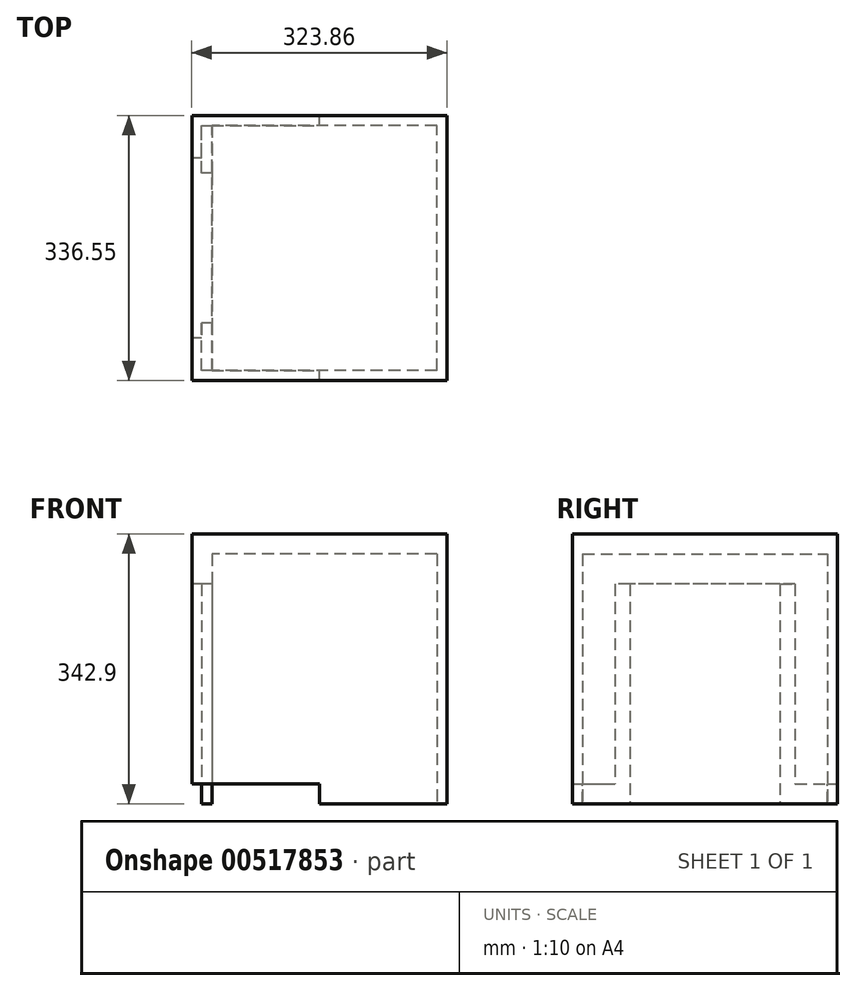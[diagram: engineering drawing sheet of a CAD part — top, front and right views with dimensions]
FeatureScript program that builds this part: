
annotation { "Feature Type Name" : "Feature", "Feature Type Description" : "" }
export const myFeature = defineFeature(function(context is Context, id is Id, definition is map)
    precondition{}
    {
        {
            var Q0;
            Q0=qCreatedBy(makeId("Top.planeOp"),FACE);
            var sketch = newSketch(context, id + "F0", { "sketchPlane" : qUnion([Q0])});
            skLineSegment(sketch, "E0.bottom", {"start": v(-161.92, 172.99) * mm, "end": v(161.92, 172.99) * mm});
            skLineSegment(sketch, "E0.top", {"start": v(-161.92, -163.56) * mm, "end": v(161.92, -163.56) * mm});
            skLineSegment(sketch, "E0.left", {"start": v(-161.92, 172.99) * mm, "end": v(-161.92, -163.56) * mm});
            skLineSegment(sketch, "E0.right", {"start": v(161.92, 172.99) * mm, "end": v(161.92, -163.56) * mm});
            skLineSegment(sketch, "E1", {"start": v(0, -163.56) * mm, "end": v(0, 172.99) * mm});
            skSolve(sketch);
        }
        {
            var Q0;
            Q0 = qSketchRegion(id + "F0", true);
            extrude(context, id + "F1", {"entities" : qUnion([Q0]), "depth" : 342.9 * mm, "offsetDistance" : 25.4 * mm});
        }
        {
            var Q0;
            Q0=makeQuery(id+"F1.opExtrude","CAP_FACE",FACE,{"disambiguationData":[OSD([sQuery(id+"F0.wireOp",EDGE,"E0.bottom"),sQuery(id+"F0.wireOp",EDGE,"E0.top"),sQuery(id+"F0.wireOp",EDGE,"E0.left"),sQuery(id+"F0.wireOp",EDGE,"E0.right")])],"isStart":true});
            var sketch = newSketch(context, id + "F2", { "sketchPlane" : qUnion([Q0])});
            skPoint(sketch, "E2.middle", {"position": v(0, 0) * mm});
            skLineSegment(sketch, "E3.bottom", {"start": v(149.22, 150.86) * mm, "end": v(-136.53, 150.86) * mm});
            skLineSegment(sketch, "E3.top", {"start": v(149.23, -160.29) * mm, "end": v(-136.52, -160.29) * mm});
            skLineSegment(sketch, "E3.left", {"start": v(149.22, 150.86) * mm, "end": v(149.23, -160.29) * mm});
            skLineSegment(sketch, "E3.right", {"start": v(-136.53, 150.86) * mm, "end": v(-136.52, -160.29) * mm});
            skSolve(sketch);
        }
        {
            var Q0;
            Q0 = qSketchRegion(id + "F2", true);
            extrude(context, id + "F3", {"entities" : qUnion([Q0]), "operationType" : NewBodyOperationType.REMOVE, "oppositeDirection" : true, "depth" : 317.5 * mm, "offsetDistance" : 25.4 * mm});
        }
        {
            var Q0;
            Q0=makeQuery(id+"F1.opExtrude","SWEPT_FACE",FACE,{"disambiguationData":[OSD([sQuery(id+"F0.wireOp",EDGE,"E0.left")])]});
            var sketch = newSketch(context, id + "F4", { "sketchPlane" : qUnion([Q0])});
            skLineSegment(sketch, "E4.bottom", {"start": v(-87.26, 222.25) * mm, "end": v(77.84, 222.25) * mm});
            skLineSegment(sketch, "E4.top", {"start": v(-87.26, 0) * mm, "end": v(77.84, 0) * mm});
            skLineSegment(sketch, "E4.left", {"start": v(-87.26, 222.25) * mm, "end": v(-87.26, 0) * mm});
            skLineSegment(sketch, "E4.right", {"start": v(77.84, 222.25) * mm, "end": v(77.84, 0) * mm});
            skSolve(sketch);
        }
        {
            var Q0;
            Q0 = qSketchRegion(id + "F4", true);
            extrude(context, id + "F5", {"entities" : qUnion([Q0]), "operationType" : NewBodyOperationType.REMOVE, "oppositeDirection" : true, "depth" : 50.8 * mm, "offsetDistance" : 25.4 * mm});
        }
        {
            var Q0;
            Q0=makeQuery(id+"F1.opExtrude","SWEPT_FACE",FACE,{"disambiguationData":[OSD([sQuery(id+"F0.wireOp",EDGE,"E0.left")])]});
            var sketch = newSketch(context, id + "F6", { "sketchPlane" : qUnion([Q0])});
            skLineSegment(sketch, "E5.bottom", {"start": v(-119.01, 279.4) * mm, "end": v(109.59, 279.4) * mm});
            skLineSegment(sketch, "E5.top", {"start": v(-119.01, 0) * mm, "end": v(109.59, 0) * mm});
            skLineSegment(sketch, "E5.left", {"start": v(-119.01, 279.4) * mm, "end": v(-119.01, 0) * mm});
            skLineSegment(sketch, "E5.right", {"start": v(109.59, 279.4) * mm, "end": v(109.59, 0) * mm});
            skSolve(sketch);
        }
        {
            var Q0;
            Q0 = qSketchRegion(id + "F6", true);
            extrude(context, id + "F7", {"entities" : qUnion([Q0]), "operationType" : NewBodyOperationType.REMOVE, "oppositeDirection" : true, "depth" : 76.2 * mm, "offsetDistance" : 25.4 * mm});
        }
        {
            var Q0;
            Q0=qCreatedBy(makeId("Right.planeOp"),FACE);
            var sketch = newSketch(context, id + "F8", { "sketchPlane" : qUnion([Q0])});
            skLineSegment(sketch, "E6.bottom", {"start": v(-172.3, 0) * mm, "end": v(183.3, 0) * mm});
            skLineSegment(sketch, "E6.top", {"start": v(-172.3, 25.4) * mm, "end": v(183.3, 25.4) * mm});
            skLineSegment(sketch, "E6.left", {"start": v(-172.3, 0) * mm, "end": v(-172.3, 25.4) * mm});
            skLineSegment(sketch, "E6.right", {"start": v(183.3, 0) * mm, "end": v(183.3, 25.4) * mm});
            skSolve(sketch);
        }
        {
            var Q0;
            Q0 = qSketchRegion(id + "F8", true);
            extrude(context, id + "F9", {"entities" : qUnion([Q0]), "operationType" : NewBodyOperationType.REMOVE, "oppositeDirection" : true, "depth" : 203.2 * mm, "offsetDistance" : 25.4 * mm});
        }
        {
            var Q0;
            Q0=makeQuery(id+"F7.boolean.opBoolean","COPY",FACE,{"derivedFrom":makeQuery(id+"F7.opExtrude","SWEPT_FACE",FACE,{"disambiguationData":[OSD([sQuery(id+"F6.wireOp",EDGE,"E5.left")])]})});
            var sketch = newSketch(context, id + "F10", { "sketchPlane" : qUnion([Q0])});
            skLineSegment(sketch, "E7.bottom", {"start": v(-136.52, 279.4) * mm, "end": v(-149.23, 279.4) * mm});
            skLineSegment(sketch, "E7.top", {"start": v(-136.52, 25.4) * mm, "end": v(-149.22, 25.4) * mm});
            skLineSegment(sketch, "E7.left", {"start": v(-136.52, 279.4) * mm, "end": v(-136.52, 25.4) * mm});
            skLineSegment(sketch, "E7.right", {"start": v(-149.23, 279.4) * mm, "end": v(-149.22, 25.4) * mm});
            skSolve(sketch);
        }
        {
            var Q0;
            Q0=makeQuery(id+"F7.boolean.opBoolean","COPY",FACE,{"derivedFrom":makeQuery(id+"F7.opExtrude","SWEPT_FACE",FACE,{"disambiguationData":[OSD([sQuery(id+"F6.wireOp",EDGE,"E5.right")])]})});
            var sketch = newSketch(context, id + "F11", { "sketchPlane" : qUnion([Q0])});
            skLineSegment(sketch, "E8.bottom", {"start": v(136.52, 279.4) * mm, "end": v(149.22, 279.4) * mm});
            skLineSegment(sketch, "E8.top", {"start": v(136.52, 25.4) * mm, "end": v(149.22, 25.4) * mm});
            skLineSegment(sketch, "E8.left", {"start": v(136.52, 279.4) * mm, "end": v(136.52, 25.4) * mm});
            skLineSegment(sketch, "E8.right", {"start": v(149.22, 279.4) * mm, "end": v(149.22, 25.4) * mm});
            skSolve(sketch);
        }
        {
            var Q0;
            Q0=makeQuery(id+"F10.imprint","IMPRINT",FACE,{"disambiguationData":[TD([[makeQuery(id+"F10.imprint","IMPRINT",EDGE,{"derivedFrom":sQuery(id+"F10.wireOp",EDGE,"E7.bottom")}),1.0]])]});
            extrude(context, id + "F12", {"entities" : qUnion([Q0]), "operationType" : NewBodyOperationType.ADD, "depth" : 19.05 * mm, "offsetDistance" : 25.4 * mm});
        }
        {
            var Q0;
            Q0=makeQuery(id+"F11.imprint","IMPRINT",FACE,{"disambiguationData":[TD([[makeQuery(id+"F11.imprint","IMPRINT",EDGE,{"derivedFrom":sQuery(id+"F11.wireOp",EDGE,"E8.bottom")}),-1.0]])]});
            var sketch = newSketch(context, id + "F13", { "sketchPlane" : qUnion([Q0])});
            skSolve(sketch);
        }
        {
            var Q0;
            Q0=makeQuery(id+"F13.imprint","IMPRINT",FACE,{"disambiguationData":[TD([[makeQuery(id+"F13.imprint","IMPRINT",EDGE,{"derivedFrom":makeQuery(id+"F11.imprint","IMPRINT",EDGE,{"derivedFrom":sQuery(id+"F11.wireOp",EDGE,"E8.bottom")})}),-1.0]])]});
            extrude(context, id + "F14", {"entities" : qUnion([Q0]), "operationType" : NewBodyOperationType.ADD, "depth" : 19.05 * mm, "offsetDistance" : 25.4 * mm});
        }
        {
            var Q0;
            {var subQ0=sQuery(id+"F8.wireOp",EDGE,"E6.top");Q0=makeQuery(id+"F14.boolean.opBoolean","MERGE",FACE,{"derivedFrom":[makeQuery(id+"F9.boolean.opBoolean","COPY",FACE,{"disambiguationData":[TD([makeQuery(id+"F1.opExtrude","SWEPT_FACE",FACE,{"disambiguationData":[OSD([sQuery(id+"F0.wireOp",EDGE,"E0.top")])]})])],"derivedFrom":makeQuery(id+"F9.opExtrude","SWEPT_FACE",FACE,{"disambiguationData":[OSD([subQ0])]})}),makeQuery(id+"F14.opExtrude","SWEPT_FACE",FACE,{"disambiguationData":[OSD([sQuery(id+"F11.wireOp",EDGE,"E8.top")])]})]});}
            var sketch = newSketch(context, id + "F15", { "sketchPlane" : qUnion([Q0])});
            skLineSegment(sketch, "E9.bottom", {"start": v(-136.53, 150.86) * mm, "end": v(-149.22, 150.86) * mm});
            skLineSegment(sketch, "E9.top", {"start": v(-136.53, 90.54) * mm, "end": v(-149.22, 90.54) * mm});
            skLineSegment(sketch, "E9.left", {"start": v(-136.53, 150.86) * mm, "end": v(-136.53, 90.54) * mm});
            skLineSegment(sketch, "E9.right", {"start": v(-149.22, 150.86) * mm, "end": v(-149.22, 90.54) * mm});
            skSolve(sketch);
        }
        {
            var Q0;
            {var subQ2=sQuery(id+"F15.wireOp",EDGE,"E9.bottom");Q0=makeQuery(id+"F15.imprint","IMPRINT",FACE,{"disambiguationData":[TD([[makeQuery(id+"F15.imprint","IMPRINT",EDGE,{"derivedFrom":subQ2}),1.0]])]});}
            extrude(context, id + "F16", {"entities" : qUnion([Q0]), "operationType" : NewBodyOperationType.ADD, "depth" : 25.4 * mm, "offsetDistance" : 25.4 * mm});
        }
        {
            var Q0;
            {var subQ0=sQuery(id+"F8.wireOp",EDGE,"E6.top");Q0=makeQuery(id+"F12.boolean.opBoolean","MERGE",FACE,{"derivedFrom":[makeQuery(id+"F9.boolean.opBoolean","COPY",FACE,{"disambiguationData":[TD([makeQuery(id+"F1.opExtrude","SWEPT_FACE",FACE,{"disambiguationData":[OSD([sQuery(id+"F0.wireOp",EDGE,"E0.bottom")])]})])],"derivedFrom":makeQuery(id+"F9.opExtrude","SWEPT_FACE",FACE,{"disambiguationData":[OSD([subQ0])]})}),makeQuery(id+"F12.opExtrude","SWEPT_FACE",FACE,{"disambiguationData":[OSD([sQuery(id+"F10.wireOp",EDGE,"E7.top")])]})]});}
            var sketch = newSketch(context, id + "F17", { "sketchPlane" : qUnion([Q0])});
            skLineSegment(sketch, "E10.bottom", {"start": v(-149.22, -99.96) * mm, "end": v(-136.52, -99.96) * mm});
            skLineSegment(sketch, "E10.top", {"start": v(-149.22, -160.29) * mm, "end": v(-136.52, -160.29) * mm});
            skLineSegment(sketch, "E10.left", {"start": v(-149.22, -99.96) * mm, "end": v(-149.22, -160.29) * mm});
            skLineSegment(sketch, "E10.right", {"start": v(-136.52, -99.96) * mm, "end": v(-136.52, -160.29) * mm});
            skSolve(sketch);
        }
        {
            var Q0;
            {var subQ1=sQuery(id+"F17.wireOp",EDGE,"E10.bottom");Q0=makeQuery(id+"F17.imprint","IMPRINT",FACE,{"disambiguationData":[TD([[makeQuery(id+"F17.imprint","IMPRINT",EDGE,{"derivedFrom":subQ1}),1.0]])]});}
            extrude(context, id + "F18", {"entities" : qUnion([Q0]), "operationType" : NewBodyOperationType.ADD, "depth" : 25.4 * mm, "offsetDistance" : 25.4 * mm});
        }
    });
